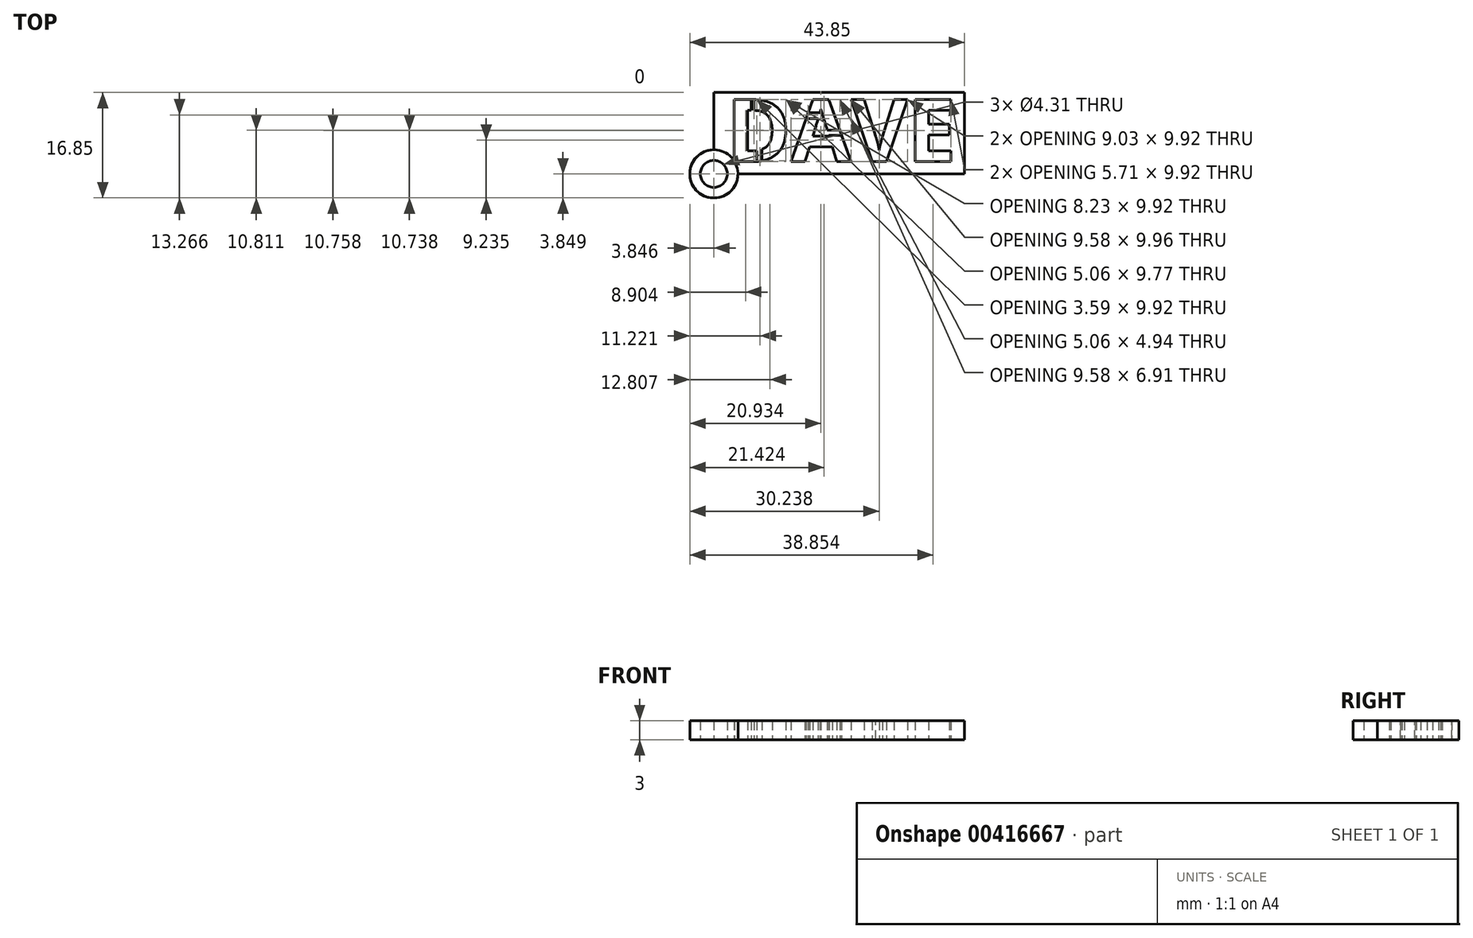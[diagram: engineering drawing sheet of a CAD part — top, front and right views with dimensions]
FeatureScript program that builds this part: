
annotation { "Feature Type Name" : "Feature", "Feature Type Description" : "" }
export const myFeature = defineFeature(function(context is Context, id is Id, definition is map)
    precondition{}
    {
        {
            var Q0;
            Q0=qCreatedBy(makeId("Top.planeOp"),FACE);
            var sketch = newSketch(context, id + "F0", { "sketchPlane" : qUnion([Q0])});
            skLineSegment(sketch, "E0.bottom", {"start": v(-31.08, 2.32) * mm, "end": v(8.92, 2.32) * mm});
            skLineSegment(sketch, "E0.top", {"start": v(-27.24, -10.68) * mm, "end": v(8.92, -10.68) * mm});
            skLineSegment(sketch, "E0.left", {"start": v(-31.08, 2.32) * mm, "end": v(-31.08, -6.84) * mm});
            skLineSegment(sketch, "E0.right", {"start": v(8.92, 2.32) * mm, "end": v(8.92, -10.68) * mm});
            skCircle(sketch, "E1", {"center": v(-31.08, -10.68) * mm, "radius": 3.84 * mm});
            skCircle(sketch, "E2", {"center": v(-31.08, -10.68) * mm, "radius": 2.16 * mm});
            skText(sketch, "E3", { "text": "DAVE", "fontName": "OpenSans-Bold.ttf"});
            skLineSegment(sketch, "E4", {"start": v(-13.08, -4.5) * mm, "end": v(-10.06, -4.5) * mm});
            skLineSegment(sketch, "E5", {"start": v(-10.06, -3.74) * mm, "end": v(-13.5, -3.74) * mm});
            skLineSegment(sketch, "E6", {"start": v(-14.13, -0.93) * mm, "end": v(-16.58, -0.93) * mm});
            skLineSegment(sketch, "E7", {"start": v(-16.86, -1.84) * mm, "end": v(-13.64, -1.84) * mm});
            skLineSegment(sketch, "E8", {"start": v(-25.14, -0.72) * mm, "end": v(-25.14, 1.25) * mm});
            skLineSegment(sketch, "E9", {"start": v(-24.65, 1.25) * mm, "end": v(-24.65, -0.79) * mm});
            skLineSegment(sketch, "E10", {"start": v(-23.39, -6.33) * mm, "end": v(-23.39, -8.75) * mm});
            skLineSegment(sketch, "E11", {"start": v(-24.23, -8.75) * mm, "end": v(-24.23, -6.54) * mm});
            skLineSegment(sketch, "E12", {"start": v(-4.52, -6.05) * mm, "end": v(-2.41, -7.94) * mm});
            skLineSegment(sketch, "E13", {"start": v(-2.48, -7.1) * mm, "end": v(-4.52, -5.27) * mm});
            const initialGuessF0  = {"E3": [-0.02907, -0.00875, 1, 0, 0.01]};
            skSetInitialGuess(sketch, initialGuessF0);
            skSolve(sketch);
        }
        {
            var Q0;
            {var subQ4=sQuery(id+"F0.wireOp",EDGE,"E3.sketch_text.stroke-7");Q0=makeQuery(id+"F0.imprint","IMPRINT",FACE,{"disambiguationData":[TD([[makeQuery(id+"F0.imprint","IMPRINT",EDGE,{"derivedFrom":subQ4}),1.0]])]});}
            var Q1;
            {var subQ1=sQuery(id+"F0.wireOp",EDGE,"E3.sketch_text.stroke-4");var subQ7=sQuery(id+"F0.wireOp",EDGE,"E3.sketch_text.stroke-5");var subQ8=makeQuery(id+"F0.imprint","INTERSECT",VERTEX,{"derivedFrom":[subQ1,subQ7]});Q1=makeQuery(id+"F0.imprint","IMPRINT",FACE,{"disambiguationData":[TD([[makeQuery(id+"F0.imprint","IMPRINT",EDGE,{"disambiguationData":[TD([[subQ8,1.0]])],"derivedFrom":subQ1}),-1.0]])]});}
            var Q2;
            {var subQ0=sQuery(id+"F0.wireOp",EDGE,"E10");var subQ1=sQuery(id+"F0.wireOp",EDGE,"E3.sketch_text.stroke-1");var subQ2=makeQuery(id+"F0.imprint","INTERSECT",VERTEX,{"derivedFrom":[subQ1,subQ0]});Q2=makeQuery(id+"F0.imprint","IMPRINT",FACE,{"disambiguationData":[TD([[makeQuery(id+"F0.imprint","IMPRINT",EDGE,{"disambiguationData":[TD([[subQ2,-1.0]])],"derivedFrom":subQ1}),-1.0]])]});}
            var Q3;
            {var subQ0=sQuery(id+"F0.wireOp",EDGE,"E3.sketch_text.stroke-21");Q3=makeQuery(id+"F0.imprint","IMPRINT",FACE,{"disambiguationData":[TD([[makeQuery(id+"F0.imprint","IMPRINT",EDGE,{"derivedFrom":subQ0}),1.0]])]});}
            var Q4;
            {var subQ0=sQuery(id+"F0.wireOp",EDGE,"E7");var subQ1=sQuery(id+"F0.wireOp",EDGE,"E3.sketch_text.stroke-16");var subQ2=makeQuery(id+"F0.imprint","INTERSECT",VERTEX,{"derivedFrom":[subQ1,subQ0]});Q4=makeQuery(id+"F0.imprint","IMPRINT",FACE,{"disambiguationData":[TD([[makeQuery(id+"F0.imprint","IMPRINT",EDGE,{"disambiguationData":[TD([[subQ2,-1.0]])],"derivedFrom":subQ1}),-1.0]])]});}
            var Q5;
            {var subQ0=sQuery(id+"F0.wireOp",EDGE,"E5");var subQ1=sQuery(id+"F0.wireOp",EDGE,"E3.sketch_text.stroke-18");var subQ2=makeQuery(id+"F0.imprint","INTERSECT",VERTEX,{"derivedFrom":[subQ1,subQ0]});Q5=makeQuery(id+"F0.imprint","IMPRINT",FACE,{"disambiguationData":[TD([[makeQuery(id+"F0.imprint","IMPRINT",EDGE,{"disambiguationData":[TD([[subQ2,-1.0]])],"derivedFrom":subQ1}),-1.0]])]});}
            var Q6;
            Q6=makeQuery(id+"F0.imprint","IMPRINT",FACE,{"disambiguationData":[TD([[makeQuery(id+"F0.imprint","IMPRINT",EDGE,{"derivedFrom":sQuery(id+"F0.wireOp",EDGE,"E0.bottom")}),-1.0]])]});
            var Q7;
            Q7=makeQuery(id+"F0.imprint","IMPRINT",FACE,{"disambiguationData":[TD([[makeQuery(id+"F0.imprint","IMPRINT",EDGE,{"derivedFrom":sQuery(id+"F0.wireOp",EDGE,"E2")}),-1.0]])]});
            extrude(context, id + "F1", {"entities" : qUnion([Q0, Q1, Q2, Q3, Q4, Q5, Q6, Q7]), "depth" : 3 * mm});
        }
        {
            var Q0;
            {var subQ0=sQuery(id+"F0.wireOp",EDGE,"5b41fa8f-4a0f-49ad-b3df-8d28d34c6c63.sketch_text.stroke-9");Q0=makeQuery(id+"F0.imprint","IMPRINT",FACE,{"disambiguationData":[TD([[makeQuery(id+"F0.imprint","IMPRINT",EDGE,{"derivedFrom":subQ0}),1.0]])]});}
            var Q1;
            {var subQ0=sQuery(id+"F0.wireOp",EDGE,"j2JYLYK2-KqMA-bHNc-Nlp2-c4o7g6eMEZB5");var subQ1=sQuery(id+"F0.wireOp",EDGE,"5b41fa8f-4a0f-49ad-b3df-8d28d34c6c63.sketch_text.stroke-6");var subQ2=makeQuery(id+"F0.imprint","INTERSECT",VERTEX,{"derivedFrom":[subQ1,subQ0]});Q1=makeQuery(id+"F0.imprint","IMPRINT",FACE,{"disambiguationData":[TD([[makeQuery(id+"F0.imprint","IMPRINT",EDGE,{"disambiguationData":[TD([[subQ2,-1.0]])],"derivedFrom":subQ1}),-1.0]])]});}
            var Q2;
            Q2=makeQuery(id+"F0.imprint","IMPRINT",FACE,{"disambiguationData":[TD([[makeQuery(id+"F0.imprint","IMPRINT",EDGE,{"derivedFrom":sQuery(id+"F0.wireOp",EDGE,"5b41fa8f-4a0f-49ad-b3df-8d28d34c6c63.sketch_text.stroke-0")}),1.0]])]});
            var Q3;
            Q3=makeQuery(id+"F0.imprint","IMPRINT",FACE,{"disambiguationData":[TD([[makeQuery(id+"F0.imprint","IMPRINT",EDGE,{"derivedFrom":sQuery(id+"F0.wireOp",EDGE,"E2")}),-1.0]])]});
            var Q4;
            {var subQ0=sQuery(id+"F0.wireOp",EDGE,"rjF3wovI-7UZE-3mW9-qbxz-Q2Cd7h3QGTnd");var subQ1=sQuery(id+"F0.wireOp",EDGE,"5b41fa8f-4a0f-49ad-b3df-8d28d34c6c63.sketch_text.stroke-4");var subQ2=makeQuery(id+"F0.imprint","INTERSECT",VERTEX,{"derivedFrom":[subQ1,subQ0]});Q4=makeQuery(id+"F0.imprint","IMPRINT",FACE,{"disambiguationData":[TD([[makeQuery(id+"F0.imprint","IMPRINT",EDGE,{"disambiguationData":[TD([[subQ2,-1.0]])],"derivedFrom":subQ1}),-1.0]])]});}
            extrude(context, id + "F2", {"entities" : qUnion([Q0, Q1, Q2, Q3, Q4]), "depth" : 3 * mm});
        }
        {
            var Q0;
            Q0 = qSketchRegion(id + "F0", true);
            extrude(context, id + "F3", {"entities" : qUnion([Q0]), "depth" : 3 * mm});
        }
    });
